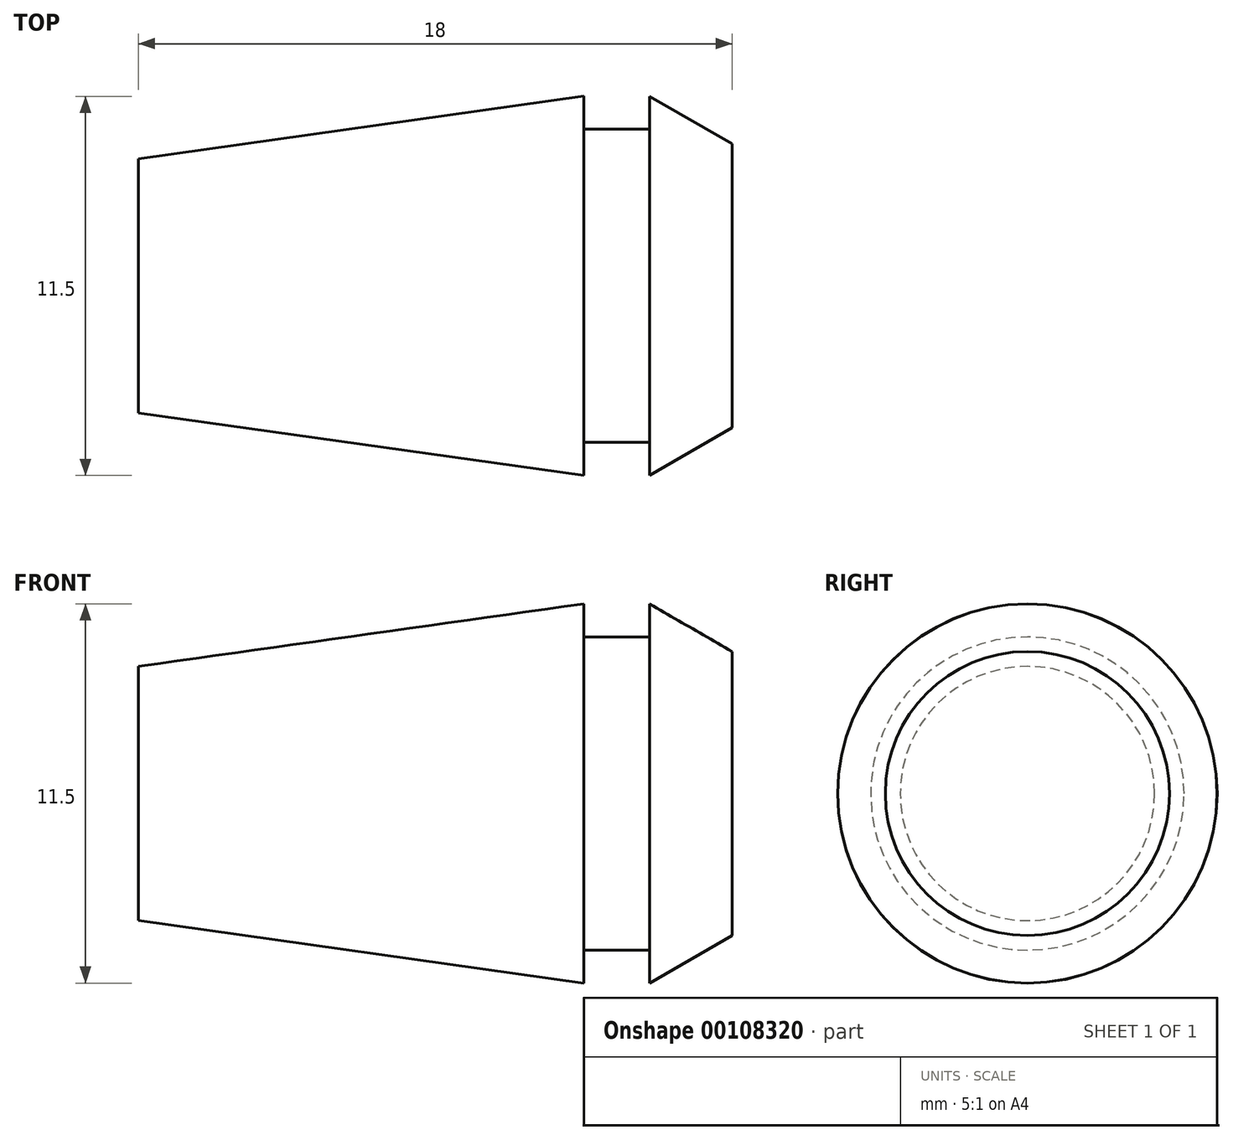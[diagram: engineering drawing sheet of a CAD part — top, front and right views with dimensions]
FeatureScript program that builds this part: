
annotation { "Feature Type Name" : "Feature", "Feature Type Description" : "" }
export const myFeature = defineFeature(function(context is Context, id is Id, definition is map)
    precondition{}
    {
        {
            var Q0;
            Q0=qCreatedBy(makeId("Top.planeOp"),FACE);
            var sketch = newSketch(context, id + "F0", { "sketchPlane" : qUnion([Q0])});
            skLineSegment(sketch, "E0", {"start": v(-18, 0) * mm, "end": v(-18, 3.86) * mm});
            skLineSegment(sketch, "E1", {"start": v(-18, 3.86) * mm, "end": v(-4.5, 5.75) * mm});
            skLineSegment(sketch, "E2", {"start": v(-4.5, 5.75) * mm, "end": v(-4.5, 4.75) * mm});
            skLineSegment(sketch, "E3", {"start": v(-4.5, 4.75) * mm, "end": v(-2.5, 4.75) * mm});
            skLineSegment(sketch, "E4", {"start": v(-2.5, 4.75) * mm, "end": v(-2.5, 5.75) * mm});
            skLineSegment(sketch, "E5", {"start": v(-2.5, 5.75) * mm, "end": v(0, 4.3) * mm});
            skLineSegment(sketch, "E6", {"start": v(0, 4.3) * mm, "end": v(0, 0) * mm});
            skLineSegment(sketch, "E7", {"start": v(-6.3, 0) * mm, "end": v(-6.3, 5.5) * mm, "construction": true});
            skLineSegment(sketch, "E8", {"start": v(-18, 0) * mm, "end": v(0, 0) * mm});
            skSolve(sketch);
        }
        {
            var Q0;
            Q0=makeQuery(id+"F0.imprint","IMPRINT",FACE,{"disambiguationData":[TD([[makeQuery(id+"F0.imprint","IMPRINT",EDGE,{"derivedFrom":sQuery(id+"F0.wireOp",EDGE,"E0")}),-1.0]])]});
            var Q1;
            Q1=sQuery(id+"F0.wireOp",EDGE,"E8");
            revolve(context, id + "F1", {"entities" : qUnion([Q0]), "axis" : qUnion([Q1]), "revolveType" : RevolveType.FULL});
        }
    });
